# Revit family: Lighting_Fixture-Ceiling-Astro-Vancouver-Square
name_source: partatom
category: Lighting Fixtures
revit_build: Autodesk Revit 2015 (Build: 20140606_1530(x64)
units: mm (PartAtom-declared; Revit-internal decimal feet)

## types (2) — shared parameters
Assembly Code = D5020200
Casing Material = Astro - Steel - Chrome Finish
Class = 3
Color Filter = 16777215
Default Elevation = 1219.2 mm  [stored 4 ft]
Description = Downlight
Diffuser Bottom Thickness = 4.5 mm  [stored 0.0147638 ft]
Diffuser Round = No
Diffuser Square = Yes
Dimmable = If a suitable dimmable driver is used
Dimming Lamp Color Temperature Shift = <None>
Energy Efficiency Rating = A+
IP Rating = IP44
Lamp = LED
Lamp included = Yes
Luminaire Lamp Efficiency Rating = A+
Manufacturer = Astro Lighting Ltd, CM20 2DP
Mountable on normally flammable surfaces = Yes
Number of Poles = 1
Product Documentation = http://www.astrolighting.co.uk
Suitable for bathroom zone = Zone 2,3
Tilt Angle = -90.00°
URL = www.astrolighting.co.uk
Voltage = 230 V

## per-type parameters (varying)
| type | Apparent Load | Cut Out Depth | Cut Out Diameter | Cut Out Radius | Diffuser I R Etched | Diffuser I R Outer | Diffuser Internal Diameter | Diffuser Internal Radius | Diffuser Radius | Heat Sink Radius | Height | Length | Light Source Elevation | Mount Thickness | Photometric Web File | Support Height | Type Comments | Wattage Comments | Weight | Width |
| 5695 Vancouver 45 Square | 4 VA | 16 mm  [stored 0.0524934 ft] | 35 mm  [stored 0.114829 ft] | 17.5 mm  [stored 0.0574147 ft] | 15 mm  [stored 0.0492126 ft] | 16 mm  [stored 0.0524934 ft] | 28 mm  [stored 0.0918635 ft] | 14 mm  [stored 0.0459318 ft] | 22.5 mm  [stored 0.0738189 ft] | 11.25 mm  [stored 0.0369094 ft] | 22 mm  [stored 0.0721785 ft] | 45 mm  [stored 0.147638 ft] | 2 mm  [stored 0.00656168 ft] | 2 mm  [stored 0.00656168 ft] | 5696 VANCOUVER 45 LED.ies | 5 mm  [stored 0.0164042 ft] | -35mm dia cut out size. -Requires a 700mA constant current driver, not included | 2.3w | 0.115kg | 45 mm  [stored 0.147638 ft] |
| 5698 Vancouver 90 Square | 12 VA | 32 mm  [stored 0.104987 ft] | 76 mm  [stored 0.249344 ft] | 38 mm  [stored 0.124672 ft] | 34 mm | 35 mm  [stored 0.114829 ft] | 66 mm  [stored 0.216535 ft] | 33 mm  [stored 0.108268 ft] | 45 mm  [stored 0.147638 ft] | 22.5 mm  [stored 0.0738189 ft] | 35.5 mm  [stored 0.11647 ft] | 90 mm  [stored 0.295276 ft] | 4 mm  [stored 0.0131234 ft] | 4 mm  [stored 0.0131234 ft] | 5697 VANCOUVER 90 LED.ies | 19.5 mm  [stored 0.0639764 ft] | -76mm dia cut out size. -Requires a 350mA constant current driver, not included | 9.8w | 0.445kg | 90 mm  [stored 0.295276 ft] |

note: column(s) folded — value = type name in every type: Model

note: [stored X ft] marks values corroborated as IEEE doubles in the binary element streams (Revit-internal decimal feet)

## geometry (parser evidence)
native form markers: Sweep x1
no freeform markers — native parametric forms only
